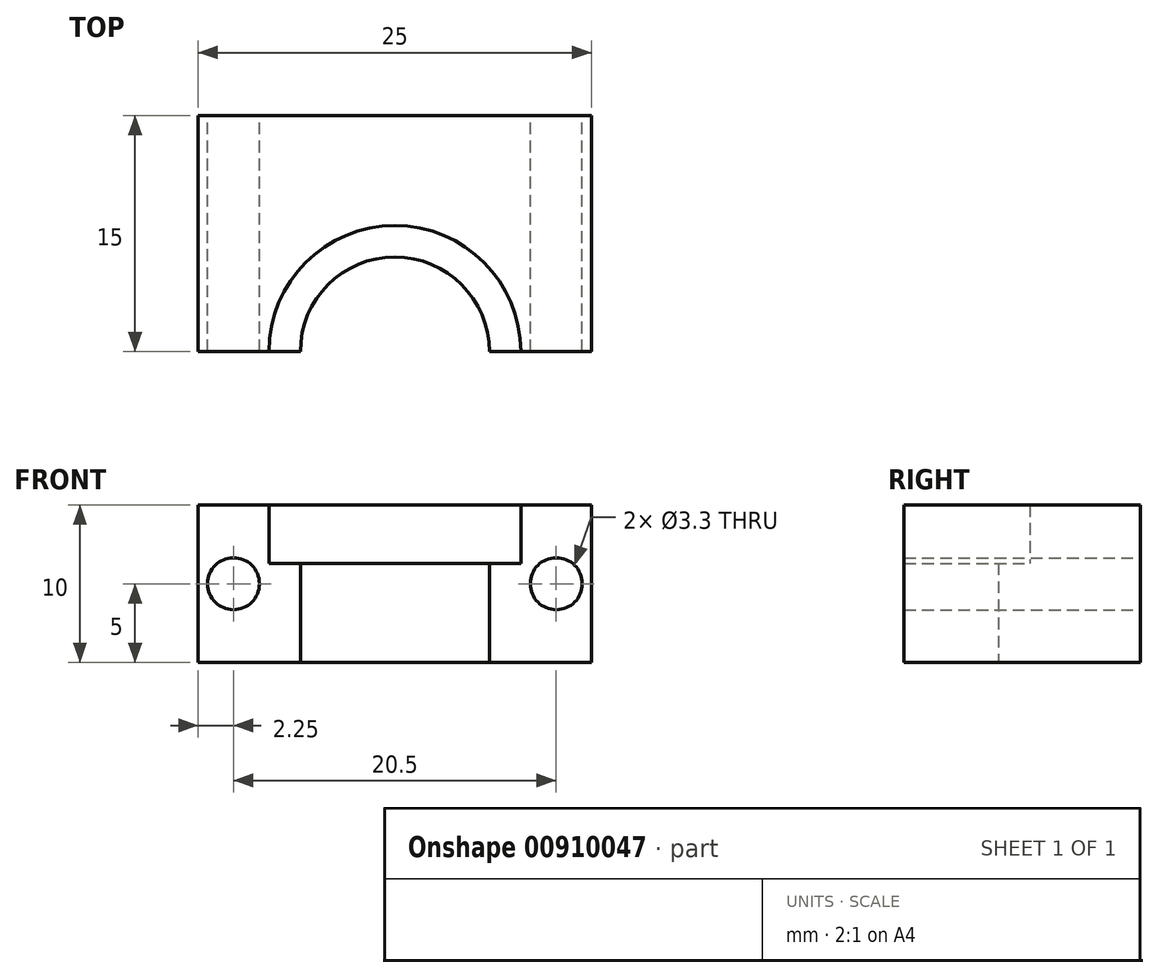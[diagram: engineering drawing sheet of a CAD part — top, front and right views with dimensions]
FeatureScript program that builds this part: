
annotation { "Feature Type Name" : "Feature", "Feature Type Description" : "" }
export const myFeature = defineFeature(function(context is Context, id is Id, definition is map)
    precondition{}
    {
        {
            var Q0;
            Q0=qCreatedBy(makeId("Top.planeOp"),FACE);
            var sketch = newSketch(context, id + "F0", { "sketchPlane" : qUnion([Q0])});
            skLineSegment(sketch, "E0.bottom", {"start": v(0, 0) * mm, "end": v(25, 0) * mm});
            skLineSegment(sketch, "E0.top", {"start": v(0, 15) * mm, "end": v(25, 15) * mm});
            skLineSegment(sketch, "E0.left", {"start": v(0, 0) * mm, "end": v(0, 15) * mm});
            skLineSegment(sketch, "E0.right", {"start": v(25, 0) * mm, "end": v(25, 15) * mm});
            skCircle(sketch, "E1", {"center": v(12.5, 0) * mm, "radius": 8 * mm});
            skCircle(sketch, "E2", {"center": v(12.5, 0) * mm, "radius": 6 * mm});
            skSolve(sketch);
        }
        {
            var Q0;
            Q0=makeQuery(id+"F0.imprint","IMPRINT",FACE,{"disambiguationData":[TD([[makeQuery(id+"F0.imprint","IMPRINT",EDGE,{"derivedFrom":sQuery(id+"F0.wireOp",EDGE,"E0.top")}),-1.0]])]});
            extrude(context, id + "F1", {"entities" : qUnion([Q0]), "depth" : 10 * mm, "offsetDistance" : 25 * mm});
        }
        {
            var Q0;
            {var subQ0=sQuery(id+"F0.wireOp",EDGE,"E1");var subQ1=sQuery(id+"F0.wireOp",EDGE,"E0.bottom");var subQ2=makeQuery(id+"F0.imprint","INTERSECT",VERTEX,{"disambiguationData":[OD(0.0)],"derivedFrom":[subQ1,subQ0]});Q0=makeQuery(id+"F0.imprint","IMPRINT",FACE,{"disambiguationData":[TD([[makeQuery(id+"F0.imprint","IMPRINT",EDGE,{"disambiguationData":[TD([[subQ2,-1.0]])],"derivedFrom":subQ1}),1.0]])]});}
            extrude(context, id + "F2", {"entities" : qUnion([Q0]), "operationType" : NewBodyOperationType.ADD, "depth" : (10 - 3.7) * mm, "offsetDistance" : 25 * mm});
        }
        {
            var Q0;
            Q0=makeQuery(id+"F1.opExtrude","SWEPT_FACE",FACE,{"disambiguationData":[OSD([sQuery(id+"F0.wireOp",EDGE,"E0.top")])]});
            var sketch = newSketch(context, id + "F3", { "sketchPlane" : qUnion([Q0])});
            skLineSegment(sketch, "E3", {"start": v(-12.5, 0) * mm, "end": v(-12.5, 5) * mm});
            skLineSegment(sketch, "E4", {"start": v(-12.5, 5) * mm, "end": v(-22.75, 5) * mm});
            skLineSegment(sketch, "E5", {"start": v(-12.5, 5) * mm, "end": v(-2.25, 5) * mm});
            skCircle(sketch, "E6", {"center": v(-22.75, 5) * mm, "radius": 1.65 * mm});
            skCircle(sketch, "E7", {"center": v(-2.25, 5) * mm, "radius": 1.65 * mm});
            skSolve(sketch);
        }
        {
            var Q0;
            Q0=makeQuery(id+"F3.imprint","IMPRINT",FACE,{"disambiguationData":[TD([[makeQuery(id+"F3.imprint","IMPRINT",EDGE,{"derivedFrom":sQuery(id+"F3.wireOp",EDGE,"E6")}),1.0]])]});
            var Q1;
            Q1=makeQuery(id+"F3.imprint","IMPRINT",FACE,{"disambiguationData":[TD([[makeQuery(id+"F3.imprint","IMPRINT",EDGE,{"derivedFrom":sQuery(id+"F3.wireOp",EDGE,"E7")}),1.0]])]});
            extrude(context, id + "F4", {"entities" : qUnion([Q0, Q1]), "operationType" : NewBodyOperationType.REMOVE, "oppositeDirection" : true, "depth" : 25 * mm, "offsetDistance" : 25 * mm});
        }
    });
